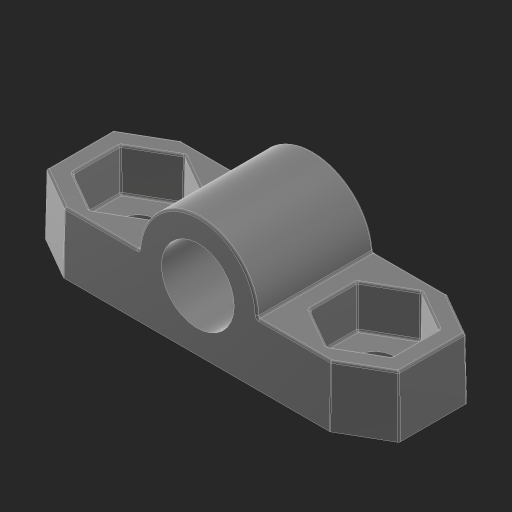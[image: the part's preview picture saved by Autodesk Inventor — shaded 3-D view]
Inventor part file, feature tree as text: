
AUTODESK INVENTOR PART (.ipt)
format: ipt  version: 2023 (Build 270158000, 158)  size: 687,104 bytes
history: native  units: in
note: dims shown in document units (in); Inventor stores cm internally (conversion verified against a paired STEP export)
features: fillet x1
ambient origin geometry x8: Origin, YZ Plane, XZ Plane, XY Plane, X Axis, Y Axis, Z Axis, Center Point
bodies: Solid1 (feature_tree)
feature tree (1):
  fillet  "Fillet7"  [1 undecoded]
note: 1 required parameter value undecoded (feature->parameter linkage not recoverable at this tier; creation-order binding heuristic only, values carry confidence <= 0.55)
